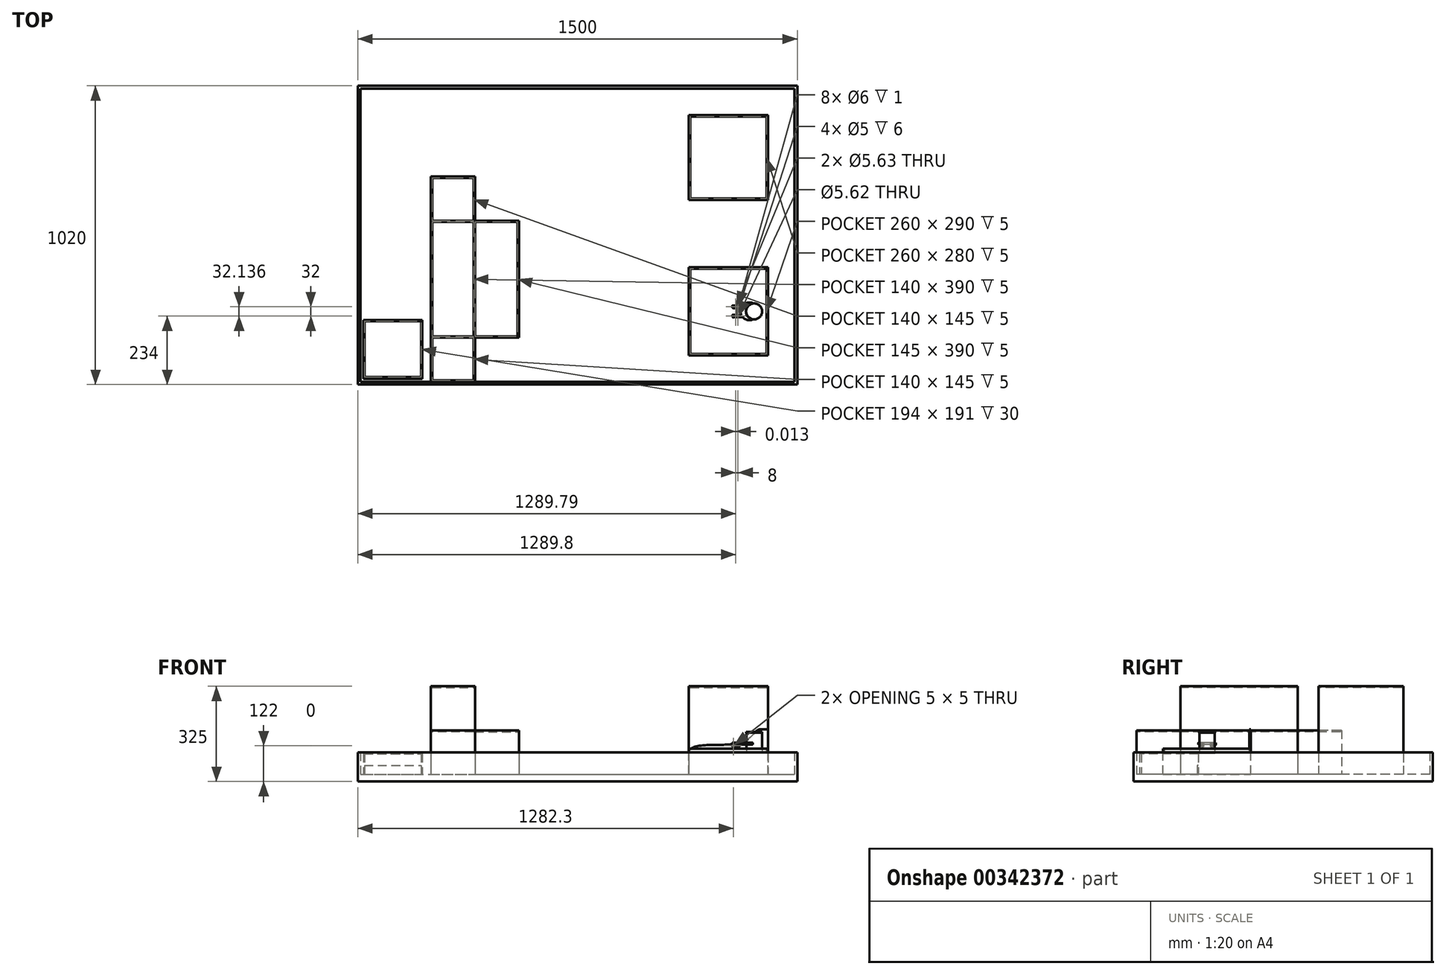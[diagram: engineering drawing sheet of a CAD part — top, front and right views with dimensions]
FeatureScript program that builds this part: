
annotation { "Feature Type Name" : "Feature", "Feature Type Description" : "" }
export const myFeature = defineFeature(function(context is Context, id is Id, definition is map)
    precondition{}
    {
        {
            var Q0;
            Q0=qCreatedBy(makeId("Top.planeOp"),FACE);
            var sketch = newSketch(context, id + "F0", { "sketchPlane" : qUnion([Q0])});
            skCircle(sketch, "E0", {"center": v(0, 0) * mm, "radius": 27.2 * mm});
            skSolve(sketch);
        }
        {
            var Q0;
            Q0=qSketchRegion(id+"F0",true);
            extrude(context, id + "F1", {"entities" : qUnion([Q0]), "depth" : 2.83 * mm});
        }
        {
            var Q0;
            Q0=makeQuery(id+"F1.opExtrude","CAP_FACE",FACE,{"disambiguationData":[OSD([sQuery(id+"F0.wireOp",EDGE,"E0")])],"isStart":false});
            var sketch = newSketch(context, id + "F2", { "sketchPlane" : qUnion([Q0])});
            skCircle(sketch, "E1", {"center": v(0, 0) * mm, "radius": 26.4 * mm});
            skSolve(sketch);
        }
        {
            var Q0;
            Q0=qSketchRegion(id+"F2",true);
            extrude(context, id + "F3", {"entities" : qUnion([Q0]), "operationType" : NewBodyOperationType.ADD, "depth" : 67.36 * mm});
        }
        {
            var Q0;
            Q0=makeQuery(id+"F3.opExtrude","CAP_FACE",FACE,{"disambiguationData":[OSD([sQuery(id+"F2.wireOp",EDGE,"E1")])],"isStart":false});
            var sketch = newSketch(context, id + "F4", { "sketchPlane" : qUnion([Q0])});
            skCircle(sketch, "E2", {"center": v(0, 0) * mm, "radius": 27.2 * mm});
            skSolve(sketch);
        }
        {
            var Q0;
            Q0=qSketchRegion(id+"F4",true);
            extrude(context, id + "F5", {"entities" : qUnion([Q0]), "operationType" : NewBodyOperationType.ADD, "depth" : 2.83 * mm});
        }
        {
            var Q0;
            Q0=makeQuery(id+"F5.opExtrude","CAP_FACE",FACE,{"disambiguationData":[OSD([sQuery(id+"F4.wireOp",EDGE,"E2")])],"isStart":false});
            var sketch = newSketch(context, id + "F6", { "sketchPlane" : qUnion([Q0])});
            skSolve(sketch);
        }
        {
            var Q0;
            Q0=qCreatedBy(makeId("Top.planeOp"),FACE);
            cPlane(context, id + "F7", {"entities" : qUnion([Q0]), "cplaneType" : CPlaneType.OFFSET, "offset" : 25 * mm, "width" : 150 * mm, "height" : 150 * mm});
        }
        {
            var Q0;
            Q0=makeQuery(id+"F6.imprint","IMPRINT",FACE,{"disambiguationData":[TD([[makeQuery(id+"F6.imprint","IMPRINT",EDGE,{"derivedFrom":makeQuery(id+"F5.opExtrude","CAP_EDGE",EDGE,{"disambiguationData":[OSD([sQuery(id+"F4.wireOp",EDGE,"E2")])],"isStart":false})}),1.0]])]});
            var sketch = newSketch(context, id + "F8", { "sketchPlane" : qUnion([Q0])});
            skSolve(sketch);
        }
        {
            var Q0;
            Q0=qCreatedBy(makeId("Top.planeOp"),FACE);
            var sketch = newSketch(context, id + "F9", { "sketchPlane" : qUnion([Q0])});
            skLineSegment(sketch, "E3.bottom", {"start": v(-222.8, -150) * mm, "end": v(47.2, -150) * mm});
            skLineSegment(sketch, "E3.top", {"start": v(-222.8, 150) * mm, "end": v(47.2, 150) * mm});
            skLineSegment(sketch, "E3.left", {"start": v(-222.8, -150) * mm, "end": v(-222.8, 150) * mm});
            skLineSegment(sketch, "E3.right", {"start": v(47.2, -150) * mm, "end": v(47.2, 150) * mm});
            skSolve(sketch);
        }
        {
            var Q0;
            Q0=qSketchRegion(id+"F9",true);
            extrude(context, id + "F10", {"entities" : qUnion([Q0]), "oppositeDirection" : true, "depth" : 72 * mm});
        }
        {
            var Q0;
            Q0=makeQuery(id+"F10.opExtrude","CAP_FACE",FACE,{"disambiguationData":[OSD([sQuery(id+"F9.wireOp",EDGE,"E3.bottom"),sQuery(id+"F9.wireOp",EDGE,"E3.top"),sQuery(id+"F9.wireOp",EDGE,"E3.left"),sQuery(id+"F9.wireOp",EDGE,"E3.right")])],"isStart":true});
            var sketch = newSketch(context, id + "F11", { "sketchPlane" : qUnion([Q0])});
            skLineSegment(sketch, "E4.bottom", {"start": v(-222.8, -150) * mm, "end": v(47.2, -150) * mm});
            skLineSegment(sketch, "E4.top", {"start": v(-222.8, -145) * mm, "end": v(42.2, -145) * mm});
            skLineSegment(sketch, "E4.left", {"start": v(-222.8, -150) * mm, "end": v(-222.8, -145) * mm});
            skLineSegment(sketch, "E5.bottom", {"start": v(47.2, 150) * mm, "end": v(42.2, 150) * mm});
            skLineSegment(sketch, "E5.left", {"start": v(47.2, 150) * mm, "end": v(47.2, -150) * mm});
            skLineSegment(sketch, "E5.right", {"start": v(42.2, 150) * mm, "end": v(42.2, -145) * mm});
            skSolve(sketch);
        }
        {
            var Q0;
            Q0=qSketchRegion(id+"F11",true);
            extrude(context, id + "F12", {"entities" : qUnion([Q0]), "operationType" : NewBodyOperationType.ADD, "depth" : 15 * mm});
        }
        {
            var Q0;
            Q0=makeQuery(id+"F12.boolean.opBoolean","MERGE",FACE,{"derivedFrom":[makeQuery(id+"F10.opExtrude","SWEPT_FACE",FACE,{"disambiguationData":[OSD([sQuery(id+"F9.wireOp",EDGE,"E3.top")])]}),makeQuery(id+"F12.opExtrude","SWEPT_FACE",FACE,{"disambiguationData":[OSD([sQuery(id+"F11.wireOp",EDGE,"E5.bottom")])]})]});
            var sketch = newSketch(context, id + "F13", { "sketchPlane" : qUnion([Q0])});
            skLineSegment(sketch, "E6", {"start": v(-47.2, 81.36) * mm, "end": v(-21.31, 81.36) * mm});
            skFitSpline(sketch, "E7", {"points": [v(-21.31, 81.36) * mm, v(15.24, 52.01) * mm, v(114.14, 28.17) * mm, v(222.8, 0) * mm], "startDerivative": vector(181.02, 0.3) * mm, "endDerivative": vector(-1.73, -239.85) * mm});
            skLineSegment(sketch, "E8", {"start": v(-47.2, 81.36) * mm, "end": v(-47.2, -72) * mm});
            skLineSegment(sketch, "E9", {"start": v(-47.2, -72) * mm, "end": v(222.8, -72) * mm});
            skLineSegment(sketch, "E10", {"start": v(222.8, -72) * mm, "end": v(222.8, 0) * mm});
            skSolve(sketch);
        }
        {
            var Q0;
            Q0=qSketchRegion(id+"F13",true);
            extrude(context, id + "F14", {"entities" : qUnion([Q0]), "operationType" : NewBodyOperationType.ADD, "oppositeDirection" : true, "depth" : 5 * mm});
        }
        {
            var Q0;
            Q0=makeQuery(id+"F10.opExtrude","CAP_FACE",FACE,{"disambiguationData":[OSD([sQuery(id+"F9.wireOp",EDGE,"E3.bottom"),sQuery(id+"F9.wireOp",EDGE,"E3.top"),sQuery(id+"F9.wireOp",EDGE,"E3.left"),sQuery(id+"F9.wireOp",EDGE,"E3.right")])],"isStart":true});
            var sketch = newSketch(context, id + "F15", { "sketchPlane" : qUnion([Q0])});
            skLineSegment(sketch, "E11.bottom", {"start": v(-222.8, 145) * mm, "end": v(-217.8, 145) * mm});
            skLineSegment(sketch, "E11.top", {"start": v(-222.8, -145) * mm, "end": v(-217.8, -145) * mm});
            skLineSegment(sketch, "E11.left", {"start": v(-222.8, 145) * mm, "end": v(-222.8, -145) * mm});
            skLineSegment(sketch, "E11.right", {"start": v(-217.8, 145) * mm, "end": v(-217.8, -145) * mm});
            skSolve(sketch);
        }
        {
            var Q0;
            Q0=qSketchRegion(id+"F15",true);
            extrude(context, id + "F16", {"entities" : qUnion([Q0]), "operationType" : NewBodyOperationType.ADD, "depth" : 5 * mm});
        }
        {
            var Q0;
            Q0=makeQuery(id+"F10.opExtrude","CAP_FACE",FACE,{"disambiguationData":[OSD([sQuery(id+"F9.wireOp",EDGE,"E3.bottom"),sQuery(id+"F9.wireOp",EDGE,"E3.top"),sQuery(id+"F9.wireOp",EDGE,"E3.left"),sQuery(id+"F9.wireOp",EDGE,"E3.right")])],"isStart":false});
            var sketch = newSketch(context, id + "F17", { "sketchPlane" : qUnion([Q0])});
            skLineSegment(sketch, "E12.bottom", {"start": v(147.2, 250) * mm, "end": v(-1352.8, 250) * mm});
            skLineSegment(sketch, "E12.top", {"start": v(147.2, -770) * mm, "end": v(-1352.8, -770) * mm});
            skLineSegment(sketch, "E12.left", {"start": v(147.2, 250) * mm, "end": v(147.2, -770) * mm});
            skLineSegment(sketch, "E12.right", {"start": v(-1352.8, 250) * mm, "end": v(-1352.8, -770) * mm});
            skSolve(sketch);
        }
        {
            var Q0;
            Q0=qSketchRegion(id+"F17",true);
            extrude(context, id + "F18", {"entities" : qUnion([Q0]), "operationType" : NewBodyOperationType.ADD, "depth" : 25 * mm});
        }
        {
            var Q0;
            Q0=makeQuery(id+"F18.opExtrude","CAP_FACE",FACE,{"disambiguationData":[OSD([sQuery(id+"F17.wireOp",EDGE,"E12.bottom"),sQuery(id+"F17.wireOp",EDGE,"E12.top"),sQuery(id+"F17.wireOp",EDGE,"E12.left"),sQuery(id+"F17.wireOp",EDGE,"E12.right")])],"isStart":true});
            var sketch = newSketch(context, id + "F19", { "sketchPlane" : qUnion([Q0])});
            skLineSegment(sketch, "E13.bottom", {"start": v(-222.8, 670) * mm, "end": v(47.2, 670) * mm});
            skLineSegment(sketch, "E13.top", {"start": v(-222.8, 380) * mm, "end": v(47.2, 380) * mm});
            skLineSegment(sketch, "E13.left", {"start": v(-222.8, 670) * mm, "end": v(-222.8, 380) * mm});
            skLineSegment(sketch, "E13.right", {"start": v(47.2, 670) * mm, "end": v(47.2, 380) * mm});
            skSolve(sketch);
        }
        {
            var Q0;
            Q0=qSketchRegion(id+"F19",true);
            extrude(context, id + "F20", {"entities" : qUnion([Q0]), "operationType" : NewBodyOperationType.ADD, "depth" : 300 * mm});
        }
        {
            var Q0;
            Q0=makeQuery(id+"F20.opExtrude","CAP_FACE",FACE,{"disambiguationData":[OSD([sQuery(id+"F19.wireOp",EDGE,"E13.bottom"),sQuery(id+"F19.wireOp",EDGE,"E13.top"),sQuery(id+"F19.wireOp",EDGE,"E13.left"),sQuery(id+"F19.wireOp",EDGE,"E13.right")])],"isStart":false});
            var sketch = newSketch(context, id + "F21", { "sketchPlane" : qUnion([Q0])});
            skLineSegment(sketch, "E14.bottom", {"start": v(-217.8, 665) * mm, "end": v(42.2, 665) * mm});
            skLineSegment(sketch, "E14.top", {"start": v(-217.8, 385) * mm, "end": v(42.2, 385) * mm});
            skLineSegment(sketch, "E14.left", {"start": v(-217.8, 665) * mm, "end": v(-217.8, 385) * mm});
            skLineSegment(sketch, "E14.right", {"start": v(42.2, 665) * mm, "end": v(42.2, 385) * mm});
            skSolve(sketch);
        }
        {
            var Q0;
            Q0=qSketchRegion(id+"F21",true);
            extrude(context, id + "F22", {"entities" : qUnion([Q0]), "operationType" : NewBodyOperationType.REMOVE, "oppositeDirection" : true, "depth" : 5 * mm});
        }
        {
            var Q0;
            Q0=makeQuery(id+"F18.opExtrude","CAP_FACE",FACE,{"disambiguationData":[OSD([sQuery(id+"F17.wireOp",EDGE,"E12.bottom"),sQuery(id+"F17.wireOp",EDGE,"E12.top"),sQuery(id+"F17.wireOp",EDGE,"E12.left"),sQuery(id+"F17.wireOp",EDGE,"E12.right")])],"isStart":true});
            var sketch = newSketch(context, id + "F23", { "sketchPlane" : qUnion([Q0])});
            skLineSegment(sketch, "E15.bottom", {"start": v(-1352.8, 770) * mm, "end": v(147.2, 770) * mm});
            skLineSegment(sketch, "E15.top", {"start": v(-1352.8, -250) * mm, "end": v(147.2, -250) * mm});
            skLineSegment(sketch, "E15.left", {"start": v(-1352.8, 770) * mm, "end": v(-1352.8, -250) * mm});
            skLineSegment(sketch, "E15.right", {"start": v(147.2, 770) * mm, "end": v(147.2, -250) * mm});
            skLineSegment(sketch, "E16.bottom", {"start": v(-1342.8, 760) * mm, "end": v(137.2, 760) * mm});
            skLineSegment(sketch, "E16.top", {"start": v(-1342.8, -240) * mm, "end": v(137.2, -240) * mm});
            skLineSegment(sketch, "E16.left", {"start": v(-1342.8, 760) * mm, "end": v(-1342.8, -240) * mm});
            skLineSegment(sketch, "E16.right", {"start": v(137.2, 760) * mm, "end": v(137.2, -240) * mm});
            skSolve(sketch);
        }
        {
            var Q0;
            Q0=qSketchRegion(id+"F23",true);
            extrude(context, id + "F24", {"entities" : qUnion([Q0]), "operationType" : NewBodyOperationType.ADD, "depth" : 75 * mm});
        }
        {
            var Q0;
            Q0=makeQuery(id+"F18.opExtrude","CAP_FACE",FACE,{"disambiguationData":[OSD([sQuery(id+"F17.wireOp",EDGE,"E12.bottom"),sQuery(id+"F17.wireOp",EDGE,"E12.top"),sQuery(id+"F17.wireOp",EDGE,"E12.left"),sQuery(id+"F17.wireOp",EDGE,"E12.right")])],"isStart":true});
            var sketch = newSketch(context, id + "F25", { "sketchPlane" : qUnion([Q0])});
            skLineSegment(sketch, "E17.bottom", {"start": v(-1102.8, 460) * mm, "end": v(-952.8, 460) * mm});
            skLineSegment(sketch, "E17.top", {"start": v(-1102.8, -240) * mm, "end": v(-952.8, -240) * mm});
            skLineSegment(sketch, "E17.left", {"start": v(-1102.8, 460) * mm, "end": v(-1102.8, -240) * mm});
            skLineSegment(sketch, "E17.right", {"start": v(-952.8, 460) * mm, "end": v(-952.8, 310) * mm});
            skLineSegment(sketch, "E18.bottom", {"start": v(-952.8, 310) * mm, "end": v(-802.8, 310) * mm});
            skLineSegment(sketch, "E18.top", {"start": v(-952.8, -90) * mm, "end": v(-802.8, -90) * mm});
            skLineSegment(sketch, "E18.right", {"start": v(-802.8, 310) * mm, "end": v(-802.8, -90) * mm});
            skLineSegment(sketch, "E19.trimOffspring", {"start": v(-952.8, -90) * mm, "end": v(-952.8, -240) * mm});
            skSolve(sketch);
        }
        {
            var Q0;
            Q0=qSketchRegion(id+"F25",true);
            extrude(context, id + "F26", {"entities" : qUnion([Q0]), "operationType" : NewBodyOperationType.ADD, "depth" : 150 * mm});
        }
        {
            var Q0;
            Q0=makeQuery(id+"F26.opExtrude","CAP_FACE",FACE,{"disambiguationData":[OSD([sQuery(id+"F25.wireOp",EDGE,"E17.bottom"),sQuery(id+"F25.wireOp",EDGE,"E17.top"),sQuery(id+"F25.wireOp",EDGE,"E17.left"),sQuery(id+"F25.wireOp",EDGE,"E17.right"),sQuery(id+"F25.wireOp",EDGE,"E18.bottom"),sQuery(id+"F25.wireOp",EDGE,"E18.top"),sQuery(id+"F25.wireOp",EDGE,"E18.right"),sQuery(id+"F25.wireOp",EDGE,"E19.trimOffspring")])],"isStart":false});
            var sketch = newSketch(context, id + "F27", { "sketchPlane" : qUnion([Q0])});
            skLineSegment(sketch, "E20.bottom", {"start": v(-952.8, 310) * mm, "end": v(-1102.8, 310) * mm});
            skLineSegment(sketch, "E20.top", {"start": v(-952.8, -90) * mm, "end": v(-1102.8, -90) * mm});
            skLineSegment(sketch, "E20.left", {"start": v(-952.8, 310) * mm, "end": v(-952.8, -90) * mm});
            skLineSegment(sketch, "E20.right", {"start": v(-1102.8, 310) * mm, "end": v(-1102.8, -90) * mm});
            skSolve(sketch);
        }
        {
            var Q0;
            Q0=qSketchRegion(id+"F27",true);
            extrude(context, id + "F28", {"entities" : qUnion([Q0]), "operationType" : NewBodyOperationType.ADD, "depth" : 150 * mm});
        }
        {
            var Q0;
            Q0=makeQuery(id+"F28.opExtrude","CAP_FACE",FACE,{"disambiguationData":[OSD([sQuery(id+"F27.wireOp",EDGE,"E20.bottom"),sQuery(id+"F27.wireOp",EDGE,"E20.top"),sQuery(id+"F27.wireOp",EDGE,"E20.left"),sQuery(id+"F27.wireOp",EDGE,"E20.right")])],"isStart":false});
            var sketch = newSketch(context, id + "F29", { "sketchPlane" : qUnion([Q0])});
            skLineSegment(sketch, "E21.bottom", {"start": v(-1097.8, 305) * mm, "end": v(-957.8, 305) * mm});
            skLineSegment(sketch, "E21.top", {"start": v(-1097.8, -85) * mm, "end": v(-957.8, -85) * mm});
            skLineSegment(sketch, "E21.left", {"start": v(-1097.8, 305) * mm, "end": v(-1097.8, -85) * mm});
            skLineSegment(sketch, "E21.right", {"start": v(-957.8, 305) * mm, "end": v(-957.8, -85) * mm});
            skSolve(sketch);
        }
        {
            var Q0;
            Q0=qSketchRegion(id+"F29",true);
            extrude(context, id + "F30", {"entities" : qUnion([Q0]), "operationType" : NewBodyOperationType.REMOVE, "oppositeDirection" : true, "depth" : 5 * mm});
        }
        {
            var Q0;
            {var subQ0=sQuery(id+"F25.wireOp",EDGE,"E17.left");var subQ1=sQuery(id+"F25.wireOp",EDGE,"E18.bottom");var subQ2=sQuery(id+"F25.wireOp",EDGE,"E17.right");var subQ3=sQuery(id+"F25.wireOp",EDGE,"E17.bottom");var subQ4=makeQuery(id+"F26.opExtrude","CAP_FACE",FACE,{"disambiguationData":[OSD([subQ3,sQuery(id+"F25.wireOp",EDGE,"E17.top"),subQ0,subQ2,subQ1,sQuery(id+"F25.wireOp",EDGE,"E18.top"),sQuery(id+"F25.wireOp",EDGE,"E18.right"),sQuery(id+"F25.wireOp",EDGE,"E19.trimOffspring")])],"isStart":false});Q0=makeQuery(id+"F28.boolean.opBoolean","SPLIT",FACE,{"disambiguationData":[TD([makeQuery(id+"F26.opExtrude","SWEPT_FACE",FACE,{"disambiguationData":[OSD([subQ3])]})])],"derivedFrom":subQ4});}
            var sketch = newSketch(context, id + "F31", { "sketchPlane" : qUnion([Q0])});
            skLineSegment(sketch, "E22.bottom", {"start": v(-1097.8, 455) * mm, "end": v(-957.8, 455) * mm});
            skLineSegment(sketch, "E22.top", {"start": v(-1097.8, 310) * mm, "end": v(-957.8, 310) * mm});
            skLineSegment(sketch, "E22.left", {"start": v(-1097.8, 455) * mm, "end": v(-1097.8, 310) * mm});
            skLineSegment(sketch, "E22.right", {"start": v(-957.8, 455) * mm, "end": v(-957.8, 310) * mm});
            skLineSegment(sketch, "E23.bottom", {"start": v(-952.8, 305) * mm, "end": v(-807.8, 305) * mm});
            skLineSegment(sketch, "E23.top", {"start": v(-952.8, -85) * mm, "end": v(-807.8, -85) * mm});
            skLineSegment(sketch, "E23.left", {"start": v(-952.8, 305) * mm, "end": v(-952.8, -85) * mm});
            skLineSegment(sketch, "E23.right", {"start": v(-807.8, 305) * mm, "end": v(-807.8, -85) * mm});
            skLineSegment(sketch, "E24.bottom", {"start": v(-1097.8, -90) * mm, "end": v(-957.8, -90) * mm});
            skLineSegment(sketch, "E24.top", {"start": v(-1097.8, -235) * mm, "end": v(-957.8, -235) * mm});
            skLineSegment(sketch, "E24.left", {"start": v(-1097.8, -90) * mm, "end": v(-1097.8, -235) * mm});
            skLineSegment(sketch, "E24.right", {"start": v(-957.8, -90) * mm, "end": v(-957.8, -235) * mm});
            skSolve(sketch);
        }
        {
            var Q0;
            Q0=qSketchRegion(id+"F31",true);
            extrude(context, id + "F32", {"entities" : qUnion([Q0]), "operationType" : NewBodyOperationType.REMOVE, "oppositeDirection" : true, "depth" : 5 * mm});
        }
        {
            var Q0;
            Q0=qCreatedBy(id+"F7.planeOp",FACE);
            var sketch = newSketch(context, id + "F33", { "sketchPlane" : qUnion([Q0])});
            skLineSegment(sketch, "E25", {"start": v(0, 0) * mm, "end": v(-90, 0) * mm, "construction": true});
            skLineSegment(sketch, "E26.bottom", {"start": v(-74.5, -12) * mm, "end": v(-55, -12) * mm});
            skLineSegment(sketch, "E26.top", {"start": v(-74.5, -20) * mm, "end": v(-55, -20) * mm});
            skLineSegment(sketch, "E26.left", {"start": v(-74.5, -12) * mm, "end": v(-74.5, -13) * mm});
            skPoint(sketch, "E27.visualSharp", {"position": v(-51, -12) * mm});
            skPoint(sketch, "E28.visualSharp", {"position": v(-51, -20) * mm});
            skCircle(sketch, "E29", {"center": v(-55, -16) * mm, "radius": 3 * mm});
            skLineSegment(sketch, "E30", {"start": v(-59, -3.98) * mm, "end": v(-59, -18.08) * mm, "construction": true});
            skCircle(sketch, "E31.MirrorC", {"center": v(-63, -16) * mm, "radius": 3 * mm});
            skLineSegment(sketch, "E32.bottom", {"start": v(-74.5, -13) * mm, "end": v(-65.65, -13) * mm});
            skLineSegment(sketch, "E32.top", {"start": v(-74.5, -19) * mm, "end": v(-65.65, -19) * mm});
            skArc(sketch, "E33", {"start": v(-65.65, -13) * mm, "mid": v(-67, -16) * mm, "end": v(-65.65, -19) * mm});
            skLineSegment(sketch, "E34.trimOffspring", {"start": v(-74.5, -19) * mm, "end": v(-74.5, -20) * mm});
            skArc(sketch, "E35.trimOffspring", {"start": v(-55, -20) * mm, "mid": v(-51, -16) * mm, "end": v(-55, -12) * mm});
            skLineSegment(sketch, "E36.MirrorCS", {"start": v(-74.5, 12) * mm, "end": v(-74.5, 13) * mm});
            skLineSegment(sketch, "E37.MirrorCS", {"start": v(-74.5, 19) * mm, "end": v(-74.5, 20) * mm});
            skPoint(sketch, "E38.MirrorP", {"position": v(-51, 12) * mm});
            skLineSegment(sketch, "E39.MirrorCS", {"start": v(-74.5, 12) * mm, "end": v(-55, 12) * mm});
            skPoint(sketch, "E40.MirrorP", {"position": v(-51, 20) * mm});
            skArc(sketch, "E41.MirrorCS", {"start": v(-65.65, 13) * mm, "mid": v(-67, 16) * mm, "end": v(-65.65, 19) * mm});
            skArc(sketch, "E42.MirrorCS", {"start": v(-55, 20) * mm, "mid": v(-51, 16) * mm, "end": v(-55, 12) * mm});
            skLineSegment(sketch, "E43.MirrorCS", {"start": v(-74.5, 20) * mm, "end": v(-55, 20) * mm});
            skCircle(sketch, "E44.MirrorC", {"center": v(-55, 16) * mm, "radius": 3 * mm});
            skCircle(sketch, "E45.MirrorC", {"center": v(-63, 16) * mm, "radius": 3 * mm});
            skLineSegment(sketch, "E46.MirrorCS", {"start": v(-74.5, 19) * mm, "end": v(-65.65, 19) * mm});
            skLineSegment(sketch, "E47.MirrorCS", {"start": v(-74.5, 13) * mm, "end": v(-65.65, 13) * mm});
            skSolve(sketch);
        }
        {
            var Q0;
            Q0=qSketchRegion(id+"F33",true);
            var Q1;
            Q1=qSketchRegion(id+"F36",true);
            extrude(context, id + "F34", {"entities" : qUnion([Q0, Q1]), "endBound" : BoundingType.SYMMETRIC, "depth" : 8 * mm});
        }
        {
            var Q0;
            Q0=makeQuery(id+"F34.opExtrude","CAP_EDGE",EDGE,{"disambiguationData":[OSD([sQuery(id+"F33.wireOp",EDGE,"E34.trimOffspring")])],"isStart":false});
            var Q1;
            Q1=makeQuery(id+"F34.opExtrude","CAP_EDGE",EDGE,{"disambiguationData":[OSD([sQuery(id+"F33.wireOp",EDGE,"E26.left")])],"isStart":false});
            var Q2;
            Q2=makeQuery(id+"F34.opExtrude","CAP_EDGE",EDGE,{"disambiguationData":[OSD([sQuery(id+"F33.wireOp",EDGE,"E34.trimOffspring")])],"isStart":true});
            var Q3;
            Q3=makeQuery(id+"F34.opExtrude","CAP_EDGE",EDGE,{"disambiguationData":[OSD([sQuery(id+"F33.wireOp",EDGE,"E26.left")])],"isStart":true});
            var Q4;
            Q4=makeQuery(id+"F34.opExtrude","CAP_EDGE",EDGE,{"disambiguationData":[OSD([sQuery(id+"F33.wireOp",EDGE,"E36.MirrorCS")])],"isStart":false});
            var Q5;
            Q5=makeQuery(id+"F34.opExtrude","CAP_EDGE",EDGE,{"disambiguationData":[OSD([sQuery(id+"F33.wireOp",EDGE,"E37.MirrorCS")])],"isStart":false});
            var Q6;
            Q6=makeQuery(id+"F34.opExtrude","CAP_EDGE",EDGE,{"disambiguationData":[OSD([sQuery(id+"F33.wireOp",EDGE,"E37.MirrorCS")])],"isStart":true});
            var Q7;
            Q7=makeQuery(id+"F34.opExtrude","CAP_EDGE",EDGE,{"disambiguationData":[OSD([sQuery(id+"F33.wireOp",EDGE,"E36.MirrorCS")])],"isStart":true});
            fillet(context, id + "F35", {"entities" : qUnion([Q0, Q1, Q2, Q3, Q4, Q5, Q6, Q7]), "radius" : 4 * mm, "tangentPropagation" : true, "allowEdgeOverflow" : false});
        }
        {
            var Q0;
            Q0=makeQuery(id+"F34.opExtrude","SWEPT_FACE",FACE,{"disambiguationData":[OSD([sQuery(id+"F33.wireOp",EDGE,"E26.top")])]});
            var sketch = newSketch(context, id + "F36", { "sketchPlane" : qUnion([Q0])});
            skCircle(sketch, "E48", {"center": v(-70.5, 25) * mm, "radius": 3 * mm});
            skSolve(sketch);
        }
        {
            var Q0;
            Q0=qSketchRegion(id+"F36",true);
            var Q1;
            Q1=makeQuery(id+"F34.opExtrude","SWEPT_FACE",FACE,{"disambiguationData":[OSD([sQuery(id+"F33.wireOp",EDGE,"E26.bottom")])]});
            extrude(context, id + "F37", {"entities" : qUnion([Q0]), "operationType" : NewBodyOperationType.ADD, "endBound" : BoundingType.UP_TO_SURFACE, "oppositeDirection" : true, "endBoundEntityFace" : qUnion([Q1]), "depth" : 25 * mm});
        }
        {
            var Q0;
            Q0=makeQuery(id+"F34.opExtrude","SWEPT_FACE",FACE,{"disambiguationData":[OSD([sQuery(id+"F33.wireOp",EDGE,"E43.MirrorCS")])]});
            var sketch = newSketch(context, id + "F38", { "sketchPlane" : qUnion([Q0])});
            skCircle(sketch, "E49", {"center": v(70.5, 25) * mm, "radius": 3 * mm});
            skSolve(sketch);
        }
        {
            var Q0;
            Q0=qSketchRegion(id+"F38",true);
            var Q1;
            Q1=makeQuery(id+"F34.opExtrude","SWEPT_FACE",FACE,{"disambiguationData":[OSD([sQuery(id+"F33.wireOp",EDGE,"E39.MirrorCS")])]});
            extrude(context, id + "F39", {"entities" : qUnion([Q0]), "operationType" : NewBodyOperationType.ADD, "endBound" : BoundingType.UP_TO_SURFACE, "oppositeDirection" : true, "endBoundEntityFace" : qUnion([Q1]), "depth" : 25 * mm});
        }
        {
            var Q0;
            Q0=qCreatedBy(id+"F7.planeOp",FACE);
            var sketch = newSketch(context, id + "F40", { "sketchPlane" : qUnion([Q0])});
            skCircle(sketch, "E50", {"center": v(-55, 16) * mm, "radius": 3 * mm});
            skCircle(sketch, "E51", {"center": v(-63, 16) * mm, "radius": 2.5 * mm});
            skCircle(sketch, "E52", {"center": v(-63, 16) * mm, "radius": 3 * mm});
            skCircle(sketch, "E53", {"center": v(-55, 16) * mm, "radius": 2.5 * mm});
            skSolve(sketch);
        }
        {
            var Q0;
            Q0=qSketchRegion(id+"F40",true);
            extrude(context, id + "F41", {"entities" : qUnion([Q0]), "operationType" : NewBodyOperationType.ADD, "endBound" : BoundingType.SYMMETRIC, "depth" : 6 * mm});
        }
        {
            var Q0;
            Q0=qCreatedBy(id+"F7.planeOp",FACE);
            var sketch = newSketch(context, id + "F42", { "sketchPlane" : qUnion([Q0])});
            skCircle(sketch, "E54", {"center": v(-63, -16) * mm, "radius": 2.5 * mm});
            skCircle(sketch, "E55", {"center": v(-63, -16) * mm, "radius": 3 * mm});
            skCircle(sketch, "E56", {"center": v(-55, -16) * mm, "radius": 2.5 * mm});
            skCircle(sketch, "E57", {"center": v(-55, -16) * mm, "radius": 3 * mm});
            skSolve(sketch);
        }
        {
            var Q0;
            Q0=qSketchRegion(id+"F42",true);
            extrude(context, id + "F43", {"entities" : qUnion([Q0]), "operationType" : NewBodyOperationType.ADD, "endBound" : BoundingType.SYMMETRIC, "depth" : 6 * mm});
        }
        {
            var Q0;
            Q0=makeQuery(id+"F34.opExtrude","SWEPT_FACE",FACE,{"disambiguationData":[OSD([sQuery(id+"F33.wireOp",EDGE,"E43.MirrorCS")])]});
            var sketch = newSketch(context, id + "F44", { "sketchPlane" : qUnion([Q0])});
            skArc(sketch, "E58", {"start": v(71.5, 27.3) * mm, "mid": v(70.5, 27.5) * mm, "end": v(69.5, 27.3) * mm});
            skLineSegment(sketch, "E59.bottom", {"start": v(68.2, 26) * mm, "end": v(69.5, 26) * mm});
            skLineSegment(sketch, "E59.top", {"start": v(68.2, 24) * mm, "end": v(69.5, 24) * mm});
            skLineSegment(sketch, "E60.left", {"start": v(71.5, 27.3) * mm, "end": v(71.5, 26) * mm});
            skLineSegment(sketch, "E60.right", {"start": v(69.5, 27.3) * mm, "end": v(69.5, 26) * mm});
            skPoint(sketch, "E61.orphan", {"position": v(69.5, 27.8) * mm});
            skPoint(sketch, "E62.orphan", {"position": v(71.5, 27.8) * mm});
            skArc(sketch, "E63.trimOffspring", {"start": v(68.2, 26) * mm, "mid": v(68, 25) * mm, "end": v(68.2, 24) * mm});
            skPoint(sketch, "E59.left.start.orphan", {"position": v(67.32, 26) * mm});
            skPoint(sketch, "E64.orphan", {"position": v(67.32, 24) * mm});
            skArc(sketch, "E65.trimOffspring", {"start": v(69.5, 22.7) * mm, "mid": v(70.5, 22.5) * mm, "end": v(71.5, 22.7) * mm});
            skLineSegment(sketch, "E66.trimOffspring", {"start": v(69.5, 24) * mm, "end": v(69.5, 22.7) * mm});
            skLineSegment(sketch, "E67.trimOffspring", {"start": v(71.5, 26) * mm, "end": v(72.8, 26) * mm});
            skLineSegment(sketch, "E68.trimOffspring", {"start": v(71.5, 24) * mm, "end": v(71.5, 22.7) * mm});
            skLineSegment(sketch, "E69.trimOffspring", {"start": v(71.5, 24) * mm, "end": v(72.8, 24) * mm});
            skPoint(sketch, "E60.top.end.orphan", {"position": v(69.5, 22.2) * mm});
            skPoint(sketch, "E70.orphan", {"position": v(71.5, 22.2) * mm});
            skPoint(sketch, "E59.right.end.orphan", {"position": v(73.68, 24) * mm});
            skPoint(sketch, "E71.orphan", {"position": v(73.68, 26) * mm});
            skArc(sketch, "E72.trimOffspring", {"start": v(72.8, 24) * mm, "mid": v(73, 25) * mm, "end": v(72.8, 26) * mm});
            skSolve(sketch);
        }
        {
            var Q0;
            Q0=qSketchRegion(id+"F44",true);
            extrude(context, id + "F45", {"entities" : qUnion([Q0]), "operationType" : NewBodyOperationType.REMOVE, "endBound" : BoundingType.THROUGH_ALL, "oppositeDirection" : true, "depth" : 25 * mm});
        }
        {
            var Q0;
            Q0=makeQuery(id+"F18.opExtrude","CAP_FACE",FACE,{"disambiguationData":[OSD([sQuery(id+"F17.wireOp",EDGE,"E12.bottom"),sQuery(id+"F17.wireOp",EDGE,"E12.top"),sQuery(id+"F17.wireOp",EDGE,"E12.left"),sQuery(id+"F17.wireOp",EDGE,"E12.right")])],"isStart":true});
            var sketch = newSketch(context, id + "F46", { "sketchPlane" : qUnion([Q0])});
            skLineSegment(sketch, "E73.bottom", {"start": v(-1332.8, -30) * mm, "end": v(-1132.8, -30) * mm});
            skLineSegment(sketch, "E73.top", {"start": v(-1332.8, -230) * mm, "end": v(-1132.8, -230) * mm});
            skLineSegment(sketch, "E73.left", {"start": v(-1332.8, -30) * mm, "end": v(-1332.8, -230) * mm});
            skLineSegment(sketch, "E73.right", {"start": v(-1132.8, -30) * mm, "end": v(-1132.8, -230) * mm});
            skLineSegment(sketch, "E74.bottom", {"start": v(-1329.8, -33) * mm, "end": v(-1135.8, -33) * mm});
            skLineSegment(sketch, "E74.top", {"start": v(-1329.8, -224) * mm, "end": v(-1135.8, -224) * mm});
            skLineSegment(sketch, "E74.left", {"start": v(-1329.8, -33) * mm, "end": v(-1329.8, -224) * mm});
            skLineSegment(sketch, "E74.right", {"start": v(-1135.8, -33) * mm, "end": v(-1135.8, -224) * mm});
            skSolve(sketch);
        }
        {
            var Q0;
            Q0=qSketchRegion(id+"F46",true);
            extrude(context, id + "F47", {"entities" : qUnion([Q0]), "operationType" : NewBodyOperationType.ADD, "depth" : 30 * mm});
        }
        {
            var Q0;
            Q0=makeQuery(id+"F47.opExtrude","CAP_FACE",FACE,{"disambiguationData":[OSD([sQuery(id+"F46.wireOp",EDGE,"E73.bottom"),sQuery(id+"F46.wireOp",EDGE,"E73.top"),sQuery(id+"F46.wireOp",EDGE,"E73.left"),sQuery(id+"F46.wireOp",EDGE,"E73.right"),sQuery(id+"F46.wireOp",EDGE,"E74.bottom"),sQuery(id+"F46.wireOp",EDGE,"E74.top"),sQuery(id+"F46.wireOp",EDGE,"E74.left"),sQuery(id+"F46.wireOp",EDGE,"E74.right")])],"isStart":false});
            var sketch = newSketch(context, id + "F48", { "sketchPlane" : qUnion([Q0])});
            skLineSegment(sketch, "E75.bottom", {"start": v(-1332.8, -30) * mm, "end": v(-1329.8, -30) * mm});
            skLineSegment(sketch, "E75.top", {"start": v(-1332.8, -230) * mm, "end": v(-1329.8, -230) * mm});
            skLineSegment(sketch, "E75.left", {"start": v(-1332.8, -30) * mm, "end": v(-1332.8, -230) * mm});
            skLineSegment(sketch, "E75.right", {"start": v(-1329.8, -30) * mm, "end": v(-1329.8, -224) * mm});
            skLineSegment(sketch, "E76.bottom", {"start": v(-1329.8, -230) * mm, "end": v(-1135.8, -230) * mm});
            skLineSegment(sketch, "E76.top", {"start": v(-1329.8, -224) * mm, "end": v(-1135.8, -224) * mm});
            skLineSegment(sketch, "E77.bottom", {"start": v(-1135.8, -230) * mm, "end": v(-1132.8, -230) * mm});
            skLineSegment(sketch, "E77.top", {"start": v(-1135.8, -30) * mm, "end": v(-1132.8, -30) * mm});
            skLineSegment(sketch, "E77.left", {"start": v(-1135.8, -224) * mm, "end": v(-1135.8, -30) * mm});
            skLineSegment(sketch, "E77.right", {"start": v(-1132.8, -230) * mm, "end": v(-1132.8, -30) * mm});
            skSolve(sketch);
        }
        {
            var Q0;
            Q0=qSketchRegion(id+"F48",true);
            extrude(context, id + "F49", {"entities" : qUnion([Q0]), "operationType" : NewBodyOperationType.ADD, "depth" : 40 * mm});
        }
        {
            var Q0;
            Q0=makeQuery(id+"F34.opExtrude","CAP_FACE",FACE,{"disambiguationData":[OSD([sQuery(id+"F33.wireOp",EDGE,"E26.bottom"),sQuery(id+"F33.wireOp",EDGE,"E26.top"),sQuery(id+"F33.wireOp",EDGE,"E26.left"),sQuery(id+"F33.wireOp",EDGE,"E29"),sQuery(id+"F33.wireOp",EDGE,"E31.MirrorC"),sQuery(id+"F33.wireOp",EDGE,"E32.bottom"),sQuery(id+"F33.wireOp",EDGE,"E32.top"),sQuery(id+"F33.wireOp",EDGE,"E33"),sQuery(id+"F33.wireOp",EDGE,"E34.trimOffspring"),sQuery(id+"F33.wireOp",EDGE,"E35.trimOffspring")])],"isStart":false});
            var sketch = newSketch(context, id + "F50", { "sketchPlane" : qUnion([Q0])});
            skLineSegment(sketch, "E78", {"start": v(-71.2, 19.96) * mm, "end": v(-38.76, 19.96) * mm});
            skLineSegment(sketch, "E79", {"start": v(-70.95, -20.39) * mm, "end": v(-38.76, -20) * mm});
            skArc(sketch, "E80", {"start": v(-4.09, 27.93) * mm, "mid": v(-22.94, 29.72) * mm, "end": v(-39.17, 19.96) * mm});
            skLineSegment(sketch, "E81", {"start": v(-71.2, 11.37) * mm, "end": v(-44.37, 11.37) * mm});
            skLineSegment(sketch, "E82", {"start": v(-71.08, -11.94) * mm, "end": v(-43.95, -11.94) * mm});
            skArc(sketch, "E83.trimOffspring", {"start": v(-44.37, 11.37) * mm, "mid": v(-46.5, -0.33) * mm, "end": v(-43.95, -11.94) * mm});
            skArc(sketch, "E84.trimOffspring", {"start": v(-38.76, -20) * mm, "mid": v(-23, -29.28) * mm, "end": v(-4.78, -27.8) * mm});
            skArc(sketch, "E85", {"start": v(-4.09, 27.93) * mm, "mid": v(-28.38, 0.37) * mm, "end": v(-4.78, -27.8) * mm});
            skLineSegment(sketch, "E86", {"start": v(-74.2, 16.96) * mm, "end": v(-74.2, 14.37) * mm});
            skLineSegment(sketch, "E87", {"start": v(-74.08, -15.06) * mm, "end": v(-73.98, -17.5) * mm});
            skArc(sketch, "E88.filletArc", {"start": v(-71.2, 19.96) * mm, "mid": v(-73.32, 19.08) * mm, "end": v(-74.2, 16.96) * mm});
            skArc(sketch, "E89.filletArc", {"start": v(-74.2, 14.37) * mm, "mid": v(-73.32, 12.25) * mm, "end": v(-71.2, 11.37) * mm});
            skArc(sketch, "E90.filletArc", {"start": v(-71.08, -11.94) * mm, "mid": v(-73.24, -12.86) * mm, "end": v(-74.08, -15.06) * mm});
            skArc(sketch, "E91.filletArc", {"start": v(-73.98, -17.5) * mm, "mid": v(-73.05, -19.56) * mm, "end": v(-70.95, -20.39) * mm});
            skCircle(sketch, "E92", {"center": v(-63.01, 16.14) * mm, "radius": 2.81 * mm});
            skCircle(sketch, "E93", {"center": v(-63, -16) * mm, "radius": 2.82 * mm});
            skCircle(sketch, "E94", {"center": v(-55, -16) * mm, "radius": 2.8 * mm});
            skCircle(sketch, "E95", {"center": v(-55, 16) * mm, "radius": 2.66 * mm});
            skSolve(sketch);
        }
        {
            var Q0;
            Q0 = qSketchRegion(id + "F50", true);
            extrude(context, id + "F51", {"entities" : qUnion([Q0]), "depth" : 6 * mm});
        }
    });
